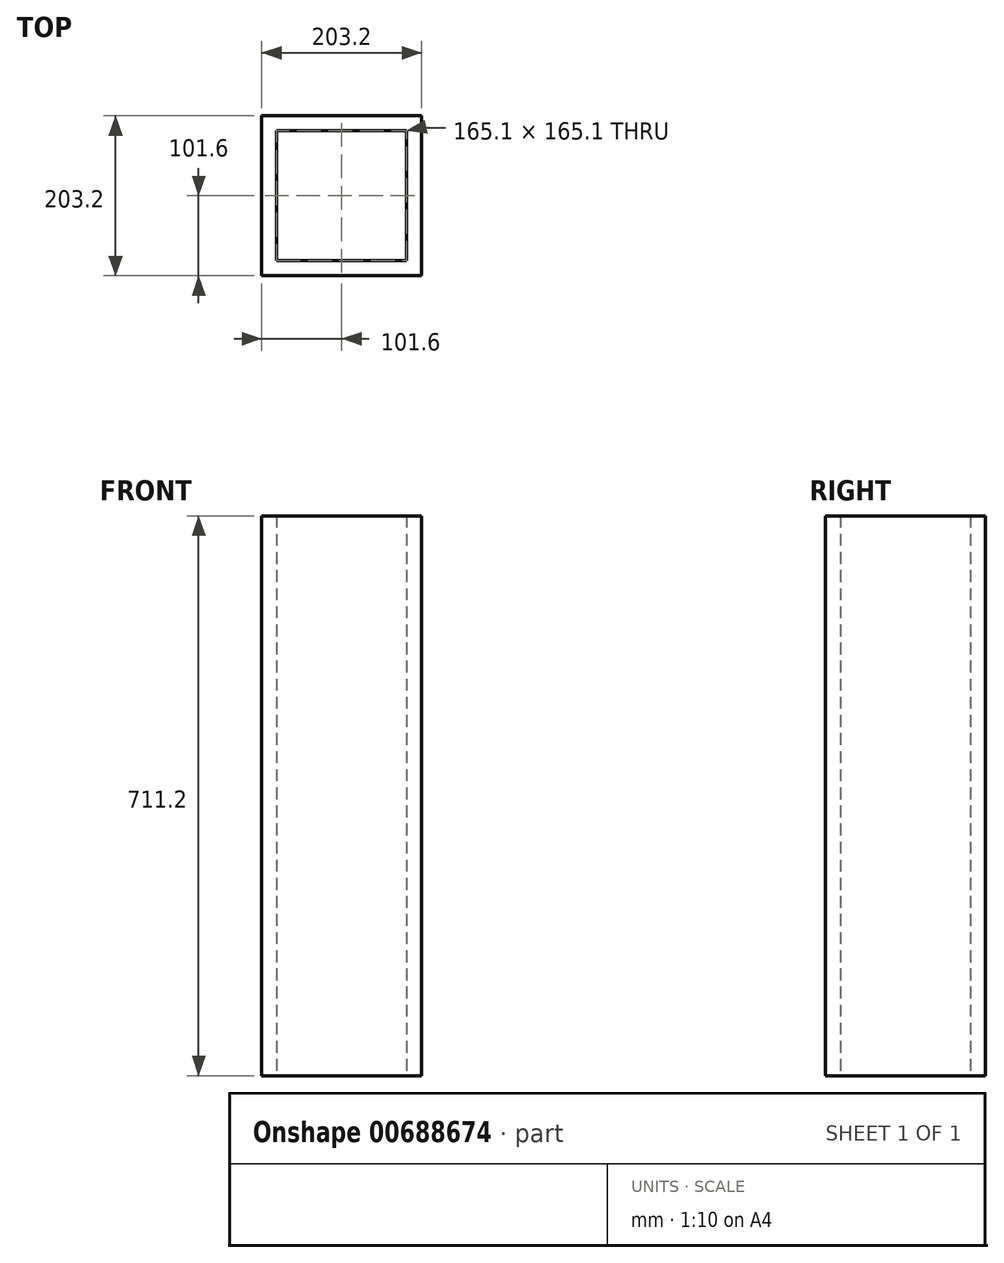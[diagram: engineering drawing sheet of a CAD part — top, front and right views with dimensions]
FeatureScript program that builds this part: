
annotation { "Feature Type Name" : "Feature", "Feature Type Description" : "" }
export const myFeature = defineFeature(function(context is Context, id is Id, definition is map)
    precondition{}
    {
        {
            var Q0;
            Q0=qCreatedBy(makeId("Top.planeOp"),FACE);
            var sketch = newSketch(context, id + "F0", { "sketchPlane" : qUnion([Q0])});
            skLineSegment(sketch, "E0.bottom", {"start": v(101.6, 101.6) * mm, "end": v(-101.6, 101.6) * mm});
            skLineSegment(sketch, "E0.top", {"start": v(101.6, -101.6) * mm, "end": v(-101.6, -101.6) * mm});
            skLineSegment(sketch, "E0.left", {"start": v(101.6, 101.6) * mm, "end": v(101.6, -101.6) * mm});
            skLineSegment(sketch, "E0.right", {"start": v(-101.6, 101.6) * mm, "end": v(-101.6, -101.6) * mm});
            skPoint(sketch, "E0.middle", {"position": v(0, 0) * mm});
            skLineSegment(sketch, "E1.bottom", {"start": v(-82.55, 82.55) * mm, "end": v(82.55, 82.55) * mm});
            skLineSegment(sketch, "E1.top", {"start": v(-82.55, -82.55) * mm, "end": v(82.55, -82.55) * mm});
            skLineSegment(sketch, "E1.left", {"start": v(-82.55, 82.55) * mm, "end": v(-82.55, -82.55) * mm});
            skLineSegment(sketch, "E1.right", {"start": v(82.55, 82.55) * mm, "end": v(82.55, -82.55) * mm});
            skSolve(sketch);
        }
        {
            var Q0;
            Q0=makeQuery(id+"F0.imprint","IMPRINT",FACE,{"disambiguationData":[TD([[makeQuery(id+"F0.imprint","IMPRINT",EDGE,{"derivedFrom":sQuery(id+"F0.wireOp",EDGE,"E0.bottom")}),1.0]])]});
            extrude(context, id + "F1", {"entities" : qUnion([Q0]), "depth" : 711.2 * mm, "offsetDistance" : 25.4 * mm});
        }
    });
